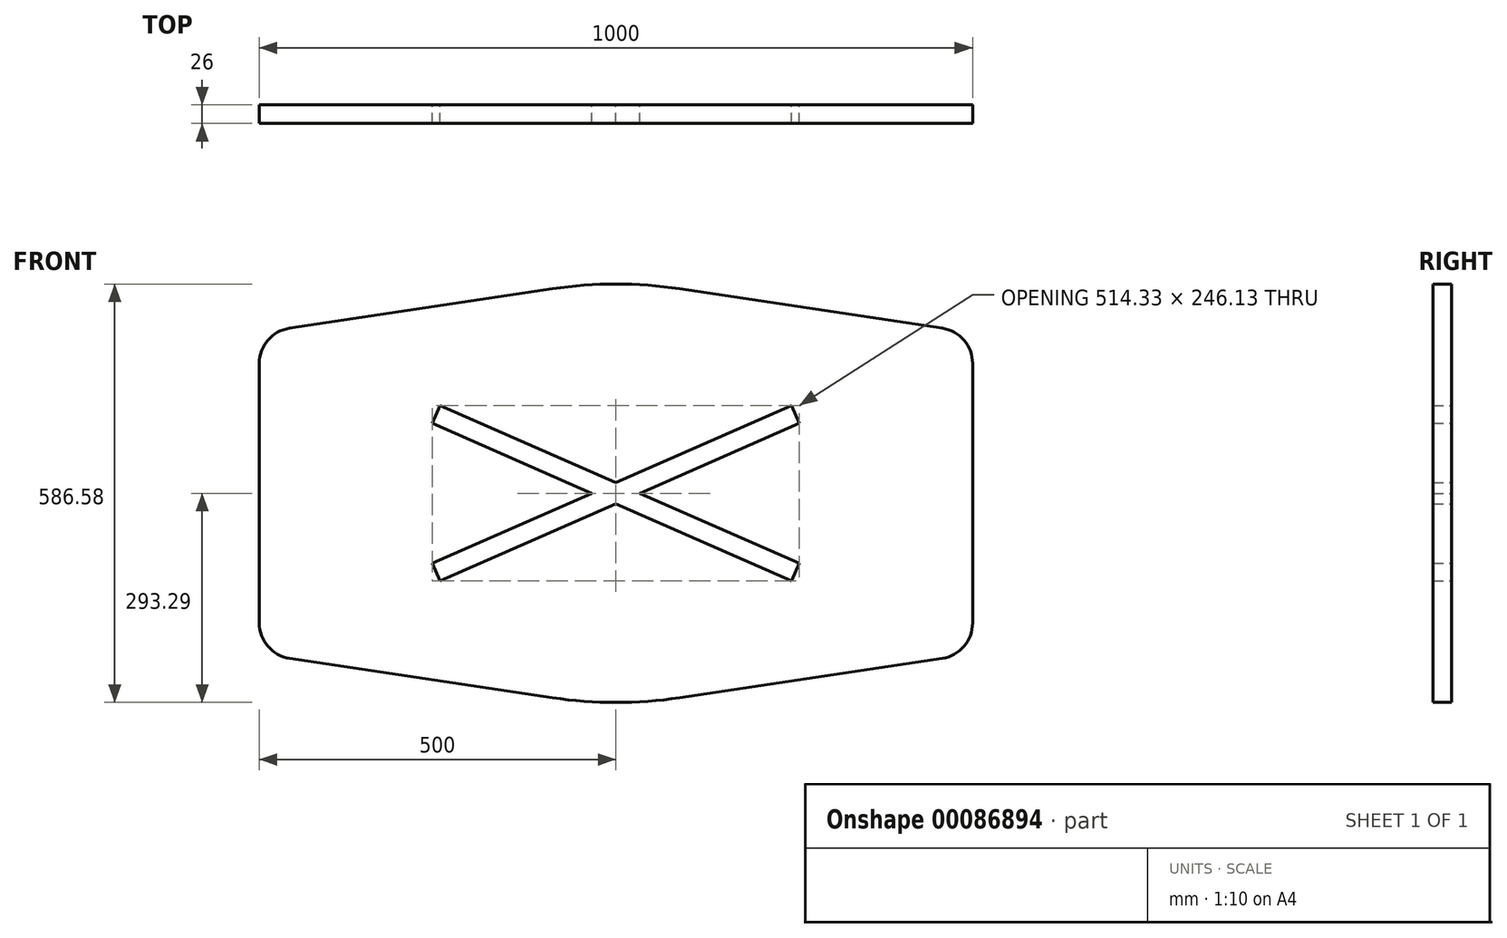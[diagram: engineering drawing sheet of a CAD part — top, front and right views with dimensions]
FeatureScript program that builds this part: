
annotation { "Feature Type Name" : "Feature", "Feature Type Description" : "" }
export const myFeature = defineFeature(function(context is Context, id is Id, definition is map)
    precondition{}
    {
        {
            var Q0;
            Q0=qCreatedBy(makeId("Front.planeOp"),FACE);
            var sketch = newSketch(context, id + "F0", { "sketchPlane" : qUnion([Q0])});
            skLineSegment(sketch, "E0", {"start": v(-500, -181.94) * mm, "end": v(-500, 181.94) * mm});
            skLineSegment(sketch, "E1", {"start": v(-457.42, 231.39) * mm, "end": v(-89, 286.65) * mm});
            skLineSegment(sketch, "E2", {"start": v(89, 286.65) * mm, "end": v(457.42, 231.39) * mm});
            skLineSegment(sketch, "E3", {"start": v(500, 181.94) * mm, "end": v(500, -181.94) * mm});
            skLineSegment(sketch, "E4", {"start": v(457.42, -231.39) * mm, "end": v(89, -286.65) * mm});
            skLineSegment(sketch, "E5", {"start": v(-89, -286.65) * mm, "end": v(-457.42, -231.39) * mm});
            skPoint(sketch, "E6.visualSharp", {"position": v(-500, 225) * mm});
            skArc(sketch, "E6.filletArc", {"start": v(-457.42, 231.39) * mm, "mid": v(-487.89, 214.57) * mm, "end": v(-500, 181.94) * mm});
            skPoint(sketch, "E7.visualSharp", {"position": v(500, 225) * mm});
            skArc(sketch, "E7.filletArc", {"start": v(500, 181.94) * mm, "mid": v(487.89, 214.57) * mm, "end": v(457.42, 231.39) * mm});
            skPoint(sketch, "E8.visualSharp", {"position": v(500, -225) * mm});
            skArc(sketch, "E8.filletArc", {"start": v(457.42, -231.39) * mm, "mid": v(487.89, -214.57) * mm, "end": v(500, -181.94) * mm});
            skPoint(sketch, "E9.visualSharp", {"position": v(-500, -225) * mm});
            skArc(sketch, "E9.filletArc", {"start": v(-500, -181.94) * mm, "mid": v(-487.89, -214.57) * mm, "end": v(-457.42, -231.39) * mm});
            skPoint(sketch, "E10.visualSharp", {"position": v(0, 300) * mm});
            skArc(sketch, "E10.filletArc", {"start": v(89, 286.65) * mm, "mid": v(0, 293.29) * mm, "end": v(-89, 286.65) * mm});
            skPoint(sketch, "E11.visualSharp", {"position": v(0, -300) * mm});
            skArc(sketch, "E11.filletArc", {"start": v(-89, -286.65) * mm, "mid": v(0, -293.29) * mm, "end": v(89, -286.65) * mm});
            skLineSegment(sketch, "E12.bottom", {"start": v(-610, 305) * mm, "end": v(610, 305) * mm, "construction": true});
            skLineSegment(sketch, "E12.top", {"start": v(-610, -305) * mm, "end": v(610, -305) * mm, "construction": true});
            skLineSegment(sketch, "E12.left", {"start": v(-610, 305) * mm, "end": v(-610, -305) * mm, "construction": true});
            skLineSegment(sketch, "E12.right", {"start": v(610, 305) * mm, "end": v(610, -305) * mm, "construction": true});
            skLineSegment(sketch, "E13", {"start": v(-487.89, 214.57) * mm, "end": v(487.89, -214.57) * mm, "construction": true});
            skLineSegment(sketch, "E14", {"start": v(-487.89, -214.57) * mm, "end": v(487.89, 214.57) * mm, "construction": true});
            skLineSegment(sketch, "E15", {"start": v(0, 14.75) * mm, "end": v(246.3, 123.07) * mm});
            skLineSegment(sketch, "E16", {"start": v(246.3, 123.07) * mm, "end": v(257.17, 98.35) * mm});
            skLineSegment(sketch, "E17", {"start": v(257.17, 98.35) * mm, "end": v(33.53, 0) * mm});
            skLineSegment(sketch, "E18", {"start": v(0, -300) * mm, "end": v(0, 306.71) * mm, "construction": true});
            skLineSegment(sketch, "E19", {"start": v(-554.48, 0) * mm, "end": v(792.75, 0) * mm, "construction": true});
            skLineSegment(sketch, "E20.MirrorCS", {"start": v(246.3, -123.07) * mm, "end": v(257.17, -98.35) * mm});
            skLineSegment(sketch, "E21.MirrorCS", {"start": v(257.17, -98.35) * mm, "end": v(33.53, 0) * mm});
            skLineSegment(sketch, "E22.MirrorCS", {"start": v(0, -14.75) * mm, "end": v(246.3, -123.07) * mm});
            skLineSegment(sketch, "E23.MirrorCS", {"start": v(-246.3, -123.07) * mm, "end": v(-257.17, -98.35) * mm});
            skLineSegment(sketch, "E24.MirrorCS", {"start": v(-246.3, 123.07) * mm, "end": v(-257.17, 98.35) * mm});
            skLineSegment(sketch, "E25.MirrorCS", {"start": v(0, -14.75) * mm, "end": v(-246.3, -123.07) * mm});
            skLineSegment(sketch, "E26.MirrorCS", {"start": v(0, 14.75) * mm, "end": v(-246.3, 123.07) * mm});
            skLineSegment(sketch, "E27", {"start": v(-257.17, -98.35) * mm, "end": v(-33.53, 0) * mm});
            skLineSegment(sketch, "E28", {"start": v(-33.53, 0) * mm, "end": v(-257.17, 98.35) * mm});
            skSolve(sketch);
        }
        {
            var Q0;
            Q0=qSketchRegion(id+"F0",true);
            extrude(context, id + "F1", {"entities" : qUnion([Q0]), "depth" : 26 * mm});
        }
    });
